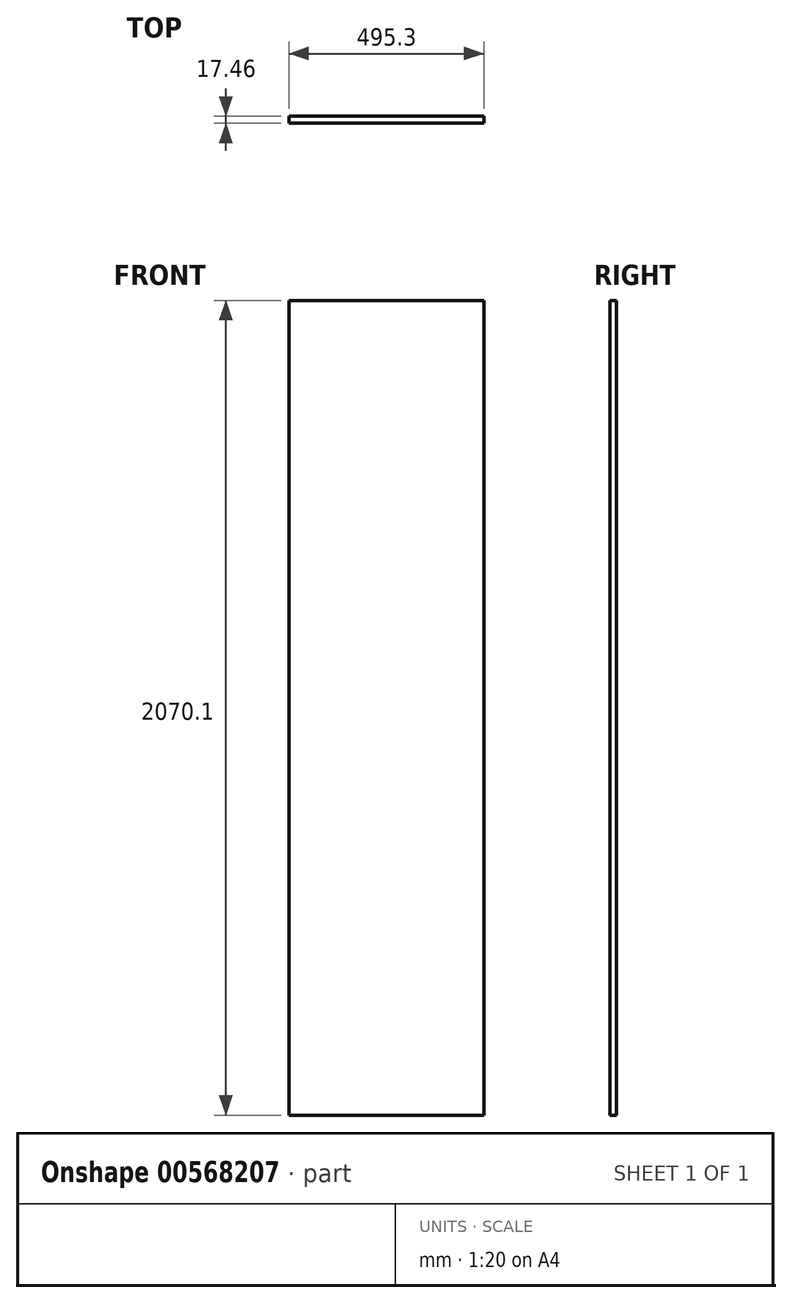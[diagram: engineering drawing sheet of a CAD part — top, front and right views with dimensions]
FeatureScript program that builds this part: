
annotation { "Feature Type Name" : "Feature", "Feature Type Description" : "" }
export const myFeature = defineFeature(function(context is Context, id is Id, definition is map)
    precondition{}
    {
        {
            var Q0;
            Q0=qCreatedBy(makeId("Front.planeOp"),FACE);
            var sketch = newSketch(context, id + "F0", { "sketchPlane" : qUnion([Q0])});
            skLineSegment(sketch, "E0.bottom", {"start": v(0, 0) * mm, "end": v(495.3, 0) * mm});
            skLineSegment(sketch, "E0.top", {"start": v(0, 2070.1) * mm, "end": v(495.3, 2070.1) * mm});
            skLineSegment(sketch, "E0.left", {"start": v(0, 0) * mm, "end": v(0, 2070.1) * mm});
            skLineSegment(sketch, "E0.right", {"start": v(495.3, 0) * mm, "end": v(495.3, 2070.1) * mm});
            skSolve(sketch);
        }
        {
            var Q0;
            Q0=makeQuery(id+"F0.imprint","IMPRINT",FACE,{"disambiguationData":[TD([[makeQuery(id+"F0.imprint","IMPRINT",EDGE,{"derivedFrom":sQuery(id+"F0.wireOp",EDGE,"E0.bottom")}),1.0]])]});
            extrude(context, id + "F1", {"entities" : qUnion([Q0]), "oppositeDirection" : true, "depth" : 17.46 * mm, "offsetDistance" : 25.4 * mm});
        }
    });
